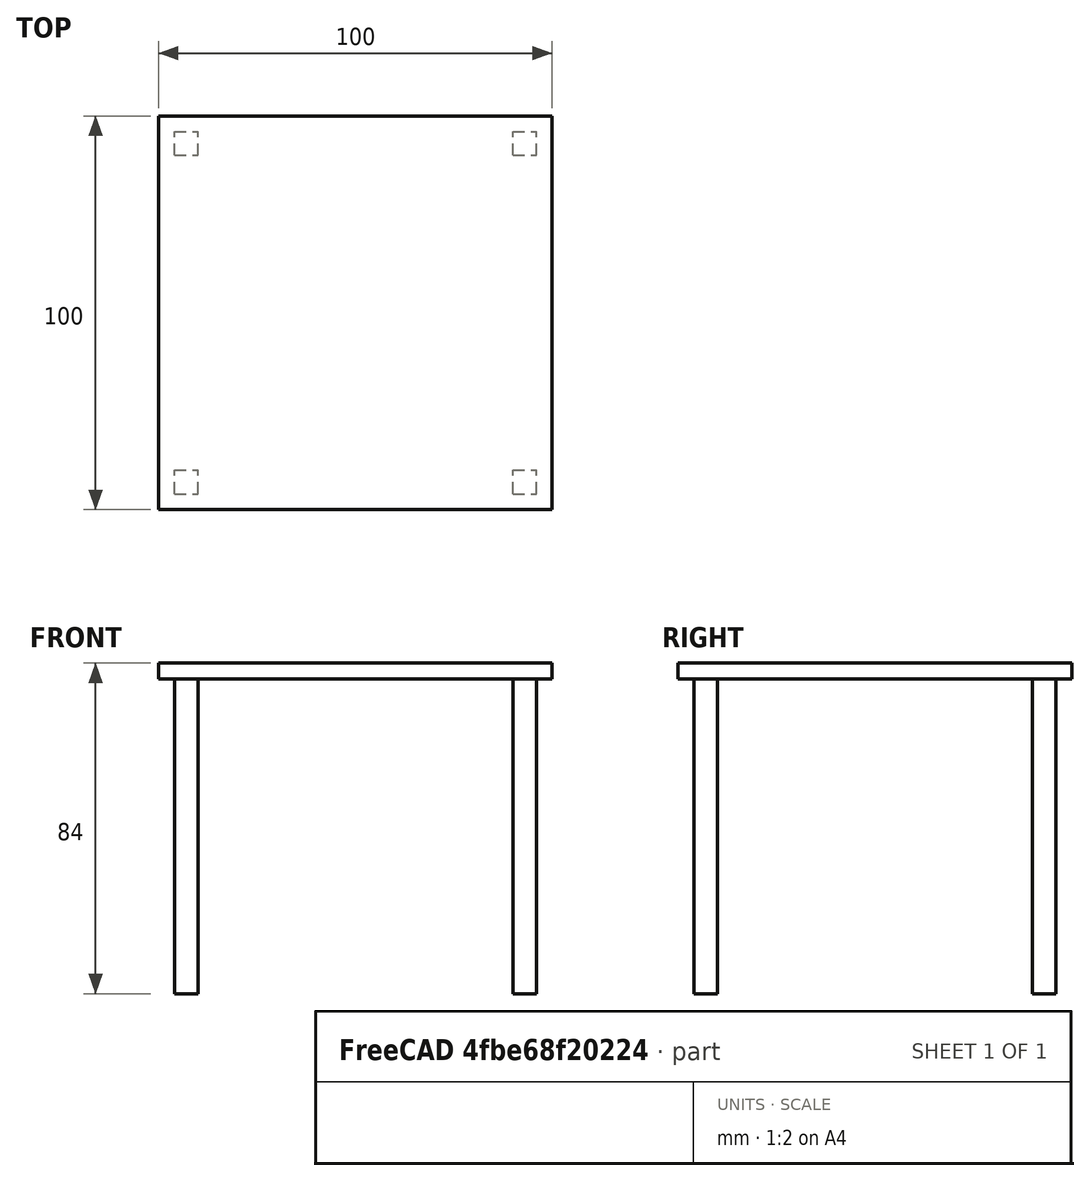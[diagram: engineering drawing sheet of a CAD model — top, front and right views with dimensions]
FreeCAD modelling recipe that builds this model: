
FCSTD DOCUMENT  (FreeCAD 0.21R33668 +26 (Git))
Label: table2
License: All rights reserved
LicenseURL: http://en.wikipedia.org/wiki/All_rights_reserved
objects: Part::Box×5
note: 5 computed .brp shape members not serialized (recipe doc carries the construction recipe); baked Part::Feature solids carry a one-line shape summary decoded from their .brp

FEATURE [Part::Box] Box  label="Cube"
  AttacherType = Attacher::AttachEngine3D
  Height = 4
  Length = 100
  Placement = pos=(0,0,80) rot=(0,0,1;0rad)
  Width = 100
FEATURE [Part::Box] Box001  label="Cube001"
  AttacherType = Attacher::AttachEngine3D
  Height = 80
  Length = 6
  Placement = pos=(4,4,0) rot=(0,0,1;0rad)
  Width = 6
FEATURE [Part::Box] Box002  label="Cube002"
  AttacherType = Attacher::AttachEngine3D
  Height = 80
  Length = 6
  Placement = pos=(90,90,0) rot=(0,0,1;0rad)
  Width = 6
FEATURE [Part::Box] Box003  label="Cube003"
  AttacherType = Attacher::AttachEngine3D
  Height = 80
  Length = 6
  Placement = pos=(4,90,0) rot=(0,0,1;0rad)
  Width = 6
FEATURE [Part::Box] Box004  label="Cube004"
  AttacherType = Attacher::AttachEngine3D
  Height = 80
  Length = 6
  Placement = pos=(90,4,0) rot=(0,0,1;0rad)
  Width = 6
